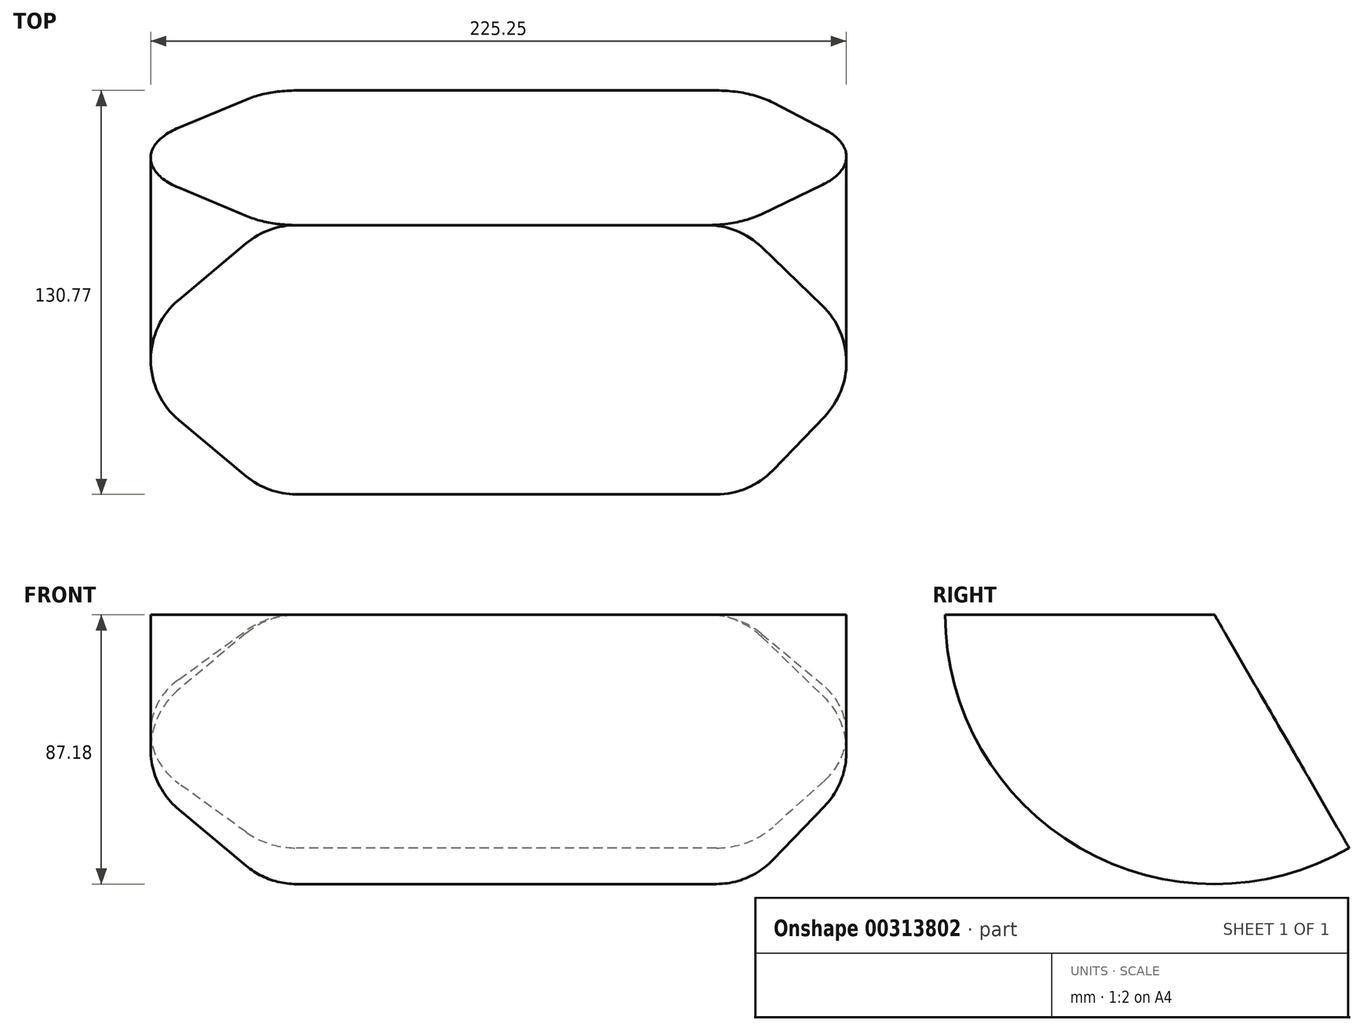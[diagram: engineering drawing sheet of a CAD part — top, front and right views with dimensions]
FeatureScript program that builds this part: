
annotation { "Feature Type Name" : "Feature", "Feature Type Description" : "" }
export const myFeature = defineFeature(function(context is Context, id is Id, definition is map)
    precondition{}
    {
        {
            var Q0;
            Q0=qCreatedBy(makeId("Top.planeOp"),FACE);
            var sketch = newSketch(context, id + "F0", { "sketchPlane" : qUnion([Q0])});
            skLineSegment(sketch, "E0", {"start": v(-76.62, 43.68) * mm, "end": v(56.31, 43.68) * mm});
            skLineSegment(sketch, "E1", {"start": v(73.93, 36.58) * mm, "end": v(93.64, 17.61) * mm});
            skLineSegment(sketch, "E2", {"start": v(94.33, -18.3) * mm, "end": v(77.59, -35.7) * mm});
            skLineSegment(sketch, "E3", {"start": v(59.28, -43.5) * mm, "end": v(-76.65, -43.5) * mm});
            skLineSegment(sketch, "E4", {"start": v(-92.92, -37.6) * mm, "end": v(-114.68, -19.47) * mm});
            skLineSegment(sketch, "E5", {"start": v(-114.72, 19.52) * mm, "end": v(-92.93, 37.76) * mm});
            skPoint(sketch, "E6.visualSharp", {"position": v(111.95, 0) * mm});
            skArc(sketch, "E6.filletArc", {"start": v(94.33, -18.3) * mm, "mid": v(101.43, -0.2) * mm, "end": v(93.64, 17.61) * mm});
            skPoint(sketch, "E7.visualSharp", {"position": v(-138.04, 0) * mm});
            skArc(sketch, "E7.filletArc", {"start": v(-114.72, 19.52) * mm, "mid": v(-123.82, 0.01) * mm, "end": v(-114.68, -19.47) * mm});
            skPoint(sketch, "E8.visualSharp", {"position": v(-85.85, 43.68) * mm});
            skArc(sketch, "E8.filletArc", {"start": v(-76.62, 43.68) * mm, "mid": v(-85.3, 42.16) * mm, "end": v(-92.93, 37.76) * mm});
            skPoint(sketch, "E9.visualSharp", {"position": v(-85.85, -43.5) * mm});
            skArc(sketch, "E9.filletArc", {"start": v(-92.92, -37.6) * mm, "mid": v(-85.3, -41.98) * mm, "end": v(-76.65, -43.5) * mm});
            skPoint(sketch, "E10.visualSharp", {"position": v(66.55, 43.68) * mm});
            skArc(sketch, "E10.filletArc", {"start": v(73.93, 36.58) * mm, "mid": v(65.8, 41.84) * mm, "end": v(56.31, 43.68) * mm});
            skPoint(sketch, "E11.visualSharp", {"position": v(70.1, -43.5) * mm});
            skArc(sketch, "E11.filletArc", {"start": v(59.28, -43.5) * mm, "mid": v(69.23, -41.47) * mm, "end": v(77.59, -35.7) * mm});
            skSolve(sketch);
        }
        {
            var Q0;
            Q0=makeQuery(id+"F0.imprint","IMPRINT",FACE,{"disambiguationData":[TD([[makeQuery(id+"F0.imprint","IMPRINT",EDGE,{"derivedFrom":sQuery(id+"F0.wireOp",EDGE,"E0")}),-1.0]])]});
            var Q1;
            Q1=sQuery(id+"F0.wireOp",EDGE,"E0");
            revolve(context, id + "F1", {"entities" : qUnion([Q0]), "axis" : qUnion([Q1]), "revolveType" : RevolveType.ONE_DIRECTION, "angle" : 120 * degree});
        }
    });
